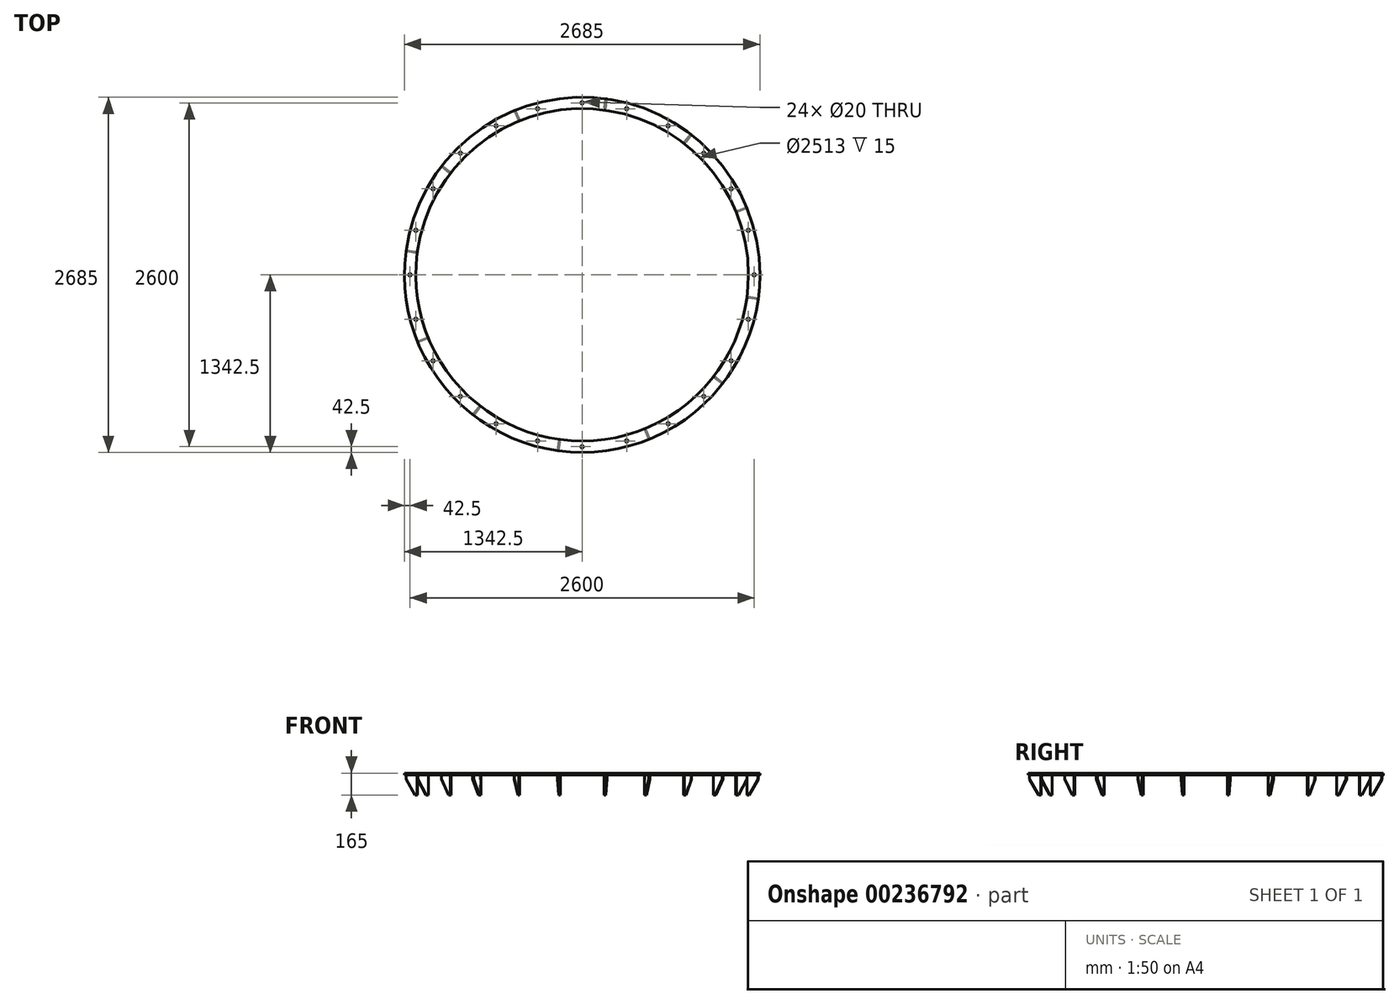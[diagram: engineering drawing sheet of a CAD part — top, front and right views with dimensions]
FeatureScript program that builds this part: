
annotation { "Feature Type Name" : "Feature", "Feature Type Description" : "" }
export const myFeature = defineFeature(function(context is Context, id is Id, definition is map)
    precondition{}
    {
        {
            var Q0;
            Q0=qCreatedBy(makeId("Top.planeOp"),FACE);
            var sketch = newSketch(context, id + "F0", { "sketchPlane" : qUnion([Q0])});
            skCircle(sketch, "E0", {"center": v(0, 0) * mm, "radius": 1342.5 * mm});
            skCircle(sketch, "E1", {"center": v(0, 0) * mm, "radius": 1256.5 * mm});
            skSolve(sketch);
        }
        {
            var Q0;
            Q0=makeQuery(id+"F0.imprint","IMPRINT",FACE,{"disambiguationData":[TD([[makeQuery(id+"F0.imprint","IMPRINT",EDGE,{"derivedFrom":sQuery(id+"F0.wireOp",EDGE,"E0")}),1.0]])]});
            extrude(context, id + "F1", {"entities" : qUnion([Q0]), "depth" : 15 * mm, "offsetDistance" : 25 * mm});
        }
        {
            var Q0;
            Q0=makeQuery(id+"F1.opExtrude","CAP_FACE",FACE,{"disambiguationData":[OSD([sQuery(id+"F0.wireOp",EDGE,"E0"),sQuery(id+"F0.wireOp",EDGE,"E1")])],"isStart":false});
            var sketch = newSketch(context, id + "F2", { "sketchPlane" : qUnion([Q0])});
            skPoint(sketch, "E2", {"position": v(0, 1300) * mm});
            skPoint(sketch, "E3.1.0", {"position": v(-336.46, 1255.7) * mm});
            skPoint(sketch, "E3.2.0", {"position": v(-650, 1125.83) * mm});
            skPoint(sketch, "E3.3.0", {"position": v(-919.24, 919.24) * mm});
            skPoint(sketch, "E3.4.0", {"position": v(-1125.83, 650) * mm});
            skPoint(sketch, "E3.5.0", {"position": v(-1255.7, 336.46) * mm});
            skPoint(sketch, "E3.6.0", {"position": v(-1300, 0) * mm});
            skPoint(sketch, "E3.7.0", {"position": v(-1255.7, -336.46) * mm});
            skPoint(sketch, "E3.8.0", {"position": v(-1125.83, -650) * mm});
            skPoint(sketch, "E3.9.0", {"position": v(-919.24, -919.24) * mm});
            skPoint(sketch, "E3.10.0", {"position": v(-650, -1125.83) * mm});
            skPoint(sketch, "E3.11.0", {"position": v(-336.46, -1255.7) * mm});
            skPoint(sketch, "E3.12.0", {"position": v(0, -1300) * mm});
            skPoint(sketch, "E3.13.0", {"position": v(336.46, -1255.7) * mm});
            skPoint(sketch, "E3.14.0", {"position": v(650, -1125.83) * mm});
            skPoint(sketch, "E3.15.0", {"position": v(919.24, -919.24) * mm});
            skPoint(sketch, "E3.16.0", {"position": v(1125.83, -650) * mm});
            skPoint(sketch, "E3.17.0", {"position": v(1255.7, -336.46) * mm});
            skPoint(sketch, "E3.18.0", {"position": v(1300, 0) * mm});
            skPoint(sketch, "E3.19.0", {"position": v(1255.7, 336.46) * mm});
            skPoint(sketch, "E3.20.0", {"position": v(1125.83, 650) * mm});
            skPoint(sketch, "E3.21.0", {"position": v(919.24, 919.24) * mm});
            skPoint(sketch, "E3.22.0", {"position": v(650, 1125.83) * mm});
            skPoint(sketch, "E3.23.0", {"position": v(336.46, 1255.7) * mm});
            skPoint(sketch, "E3.center", {"position": v(0, 0) * mm});
            skSolve(sketch);
        }
        {
            var Q0;
            Q0=sQuery(id+"F2.wireOp",VERTEX,"E2");
            var Q1;
            Q1=sQuery(id+"F2.wireOp",VERTEX,"E3.1.0");
            var Q2;
            Q2=sQuery(id+"F2.wireOp",VERTEX,"E3.2.0");
            var Q3;
            Q3=sQuery(id+"F2.wireOp",VERTEX,"E3.3.0");
            var Q4;
            Q4=sQuery(id+"F2.wireOp",VERTEX,"E3.4.0");
            var Q5;
            Q5=sQuery(id+"F2.wireOp",VERTEX,"E3.23.0");
            var Q6;
            Q6=sQuery(id+"F2.wireOp",VERTEX,"E3.22.0");
            var Q7;
            Q7=sQuery(id+"F2.wireOp",VERTEX,"E3.21.0");
            var Q8;
            Q8=sQuery(id+"F2.wireOp",VERTEX,"E3.20.0");
            var Q9;
            Q9=sQuery(id+"F2.wireOp",VERTEX,"E3.19.0");
            var Q10;
            Q10=sQuery(id+"F2.wireOp",VERTEX,"E3.18.0");
            var Q11;
            Q11=sQuery(id+"F2.wireOp",VERTEX,"E3.17.0");
            var Q12;
            Q12=sQuery(id+"F2.wireOp",VERTEX,"E3.16.0");
            var Q13;
            Q13=sQuery(id+"F2.wireOp",VERTEX,"E3.15.0");
            var Q14;
            Q14=sQuery(id+"F2.wireOp",VERTEX,"E3.14.0");
            var Q15;
            Q15=sQuery(id+"F2.wireOp",VERTEX,"E3.13.0");
            var Q16;
            Q16=sQuery(id+"F2.wireOp",VERTEX,"E3.12.0");
            var Q17;
            Q17=sQuery(id+"F2.wireOp",VERTEX,"E3.11.0");
            var Q18;
            Q18=sQuery(id+"F2.wireOp",VERTEX,"E3.10.0");
            var Q19;
            Q19=sQuery(id+"F2.wireOp",VERTEX,"E3.9.0");
            var Q20;
            Q20=sQuery(id+"F2.wireOp",VERTEX,"E3.8.0");
            var Q21;
            Q21=sQuery(id+"F2.wireOp",VERTEX,"E3.7.0");
            var Q22;
            Q22=sQuery(id+"F2.wireOp",VERTEX,"E3.6.0");
            var Q23;
            Q23=sQuery(id+"F2.wireOp",VERTEX,"E3.5.0");
            var Q24;
            Q24=makeQuery(id+"F1.opExtrude","SWEPT_BODY",BODY,{"disambiguationData":[OSD([sQuery(id+"F0.wireOp",EDGE,"E0"),sQuery(id+"F0.wireOp",EDGE,"E1")])]});
            hole(context, id + "F3", {"style" : HoleStyle.SIMPLE, "endStyle" : HoleEndStyle.THROUGH, "standardTappedOrClearance" : lookupTablePath({ "fit" : "Normal", "standard" : "ISO", "size" : "M18", "type" : "Clearance" }), "standardBlindInLast" : lookupTablePath({ "fit" : "Normal", "standard" : "ISO", "engagement" : "75%", "pitch" : "1.5 mm", "size" : "M18", "type" : "Clearance & tapped" }), "holeDiameter" : 20 * mm, "majorDiameter" : 5 * mm, "isTappedThrough" : true, "tappedDepth" : 28 * mm, "tapClearance" : 3, "locations" : qUnion([Q0, Q1, Q2, Q3, Q4, Q5, Q6, Q7, Q8, Q9, Q10, Q11, Q12, Q13, Q14, Q15, Q16, Q17, Q18, Q19, Q20, Q21, Q22, Q23]), "scope" : qUnion([Q24])});
        }
        {
            var Q0;
            Q0=makeQuery(id+"F1.opExtrude","CAP_FACE",FACE,{"disambiguationData":[OSD([sQuery(id+"F0.wireOp",EDGE,"E0"),sQuery(id+"F0.wireOp",EDGE,"E1")])],"isStart":true});
            var sketch = newSketch(context, id + "F4", { "sketchPlane" : qUnion([Q0])});
            skLineSegment(sketch, "E4", {"start": v(186.84, -1329.43) * mm, "end": v(174.87, -1244.23) * mm});
            skLineSegment(sketch, "E5", {"start": v(0, -1300) * mm, "end": v(0, 0) * mm});
            skLineSegment(sketch, "E6", {"start": v(186.84, -1329.43) * mm, "end": v(176.94, -1330.83) * mm});
            skLineSegment(sketch, "E7", {"start": v(176.94, -1330.83) * mm, "end": v(164.96, -1245.62) * mm});
            skLineSegment(sketch, "E8", {"start": v(164.96, -1245.62) * mm, "end": v(174.87, -1244.23) * mm});
            skSolve(sketch);
        }
        {
            var Q0;
            Q0=qSketchRegion(id+"F4",true);
            extrude(context, id + "F5", {"entities" : qUnion([Q0]), "depth" : 150 * mm, "offsetDistance" : 25 * mm});
        }
        {
            var Q0;
            Q0=makeQuery(id+"F5.opExtrude","CAP_EDGE",EDGE,{"disambiguationData":[OSD([sQuery(id+"F4.wireOp",EDGE,"E6")])],"isStart":false});
            chamfer(context, id + "F6", {"entities" : qUnion([Q0]), "chamferType" : ChamferType.OFFSET_ANGLE, "width" : 120 * mm, "oppositeDirection" : false, "angle" : 30 * degree, "tangentPropagation" : true});
        }
        {
            var Q0;
            Q0=makeQuery(id+"F5.opExtrude","SWEPT_BODY",BODY,{"disambiguationData":[OSD([sQuery(id+"F4.wireOp",EDGE,"E4"),sQuery(id+"F4.wireOp",EDGE,"E6"),sQuery(id+"F4.wireOp",EDGE,"E7"),sQuery(id+"F4.wireOp",EDGE,"E8")])]});
            var Q1;
            Q1=makeQuery(id+"F1.opExtrude","CAP_EDGE",EDGE,{"disambiguationData":[OSD([sQuery(id+"F0.wireOp",EDGE,"E1")])],"isStart":false});
            circularPattern(context, id + "F7", {"operationType" : NewBodyOperationType.ADD, "entities" : qUnion([Q0]), "axis" : qUnion([Q1]), "angle" : 360 * degree, "instanceCount" : 12, "equalSpace" : true, "isCentered" : true});
        }
    });
